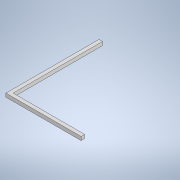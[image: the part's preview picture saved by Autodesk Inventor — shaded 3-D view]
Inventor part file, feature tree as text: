
AUTODESK INVENTOR PART (.ipt)
format: ipt  version: 2020.2 (Build 242310000, 310)  size: 103,424 bytes
history: native  units: mm
features: extrude x1, sketch x1
ambient origin geometry x8: Origin, YZ Plane, XZ Plane, XY Plane, X Axis, Y Axis, Z Axis, Center Point
bodies: Solid1 (feature_tree)
feature tree (2):
  extrude  "Extrusion1"  Depth=2000.0mm
  sketch  "Sketch1"  dims[d0=5000.0mm d1=5000.0mm d3=100.0mm d4=0.0mm d7=2500.0mm d8=100.0mm d9=100.0mm d10=2000.0mm d11=2000.0mm]
